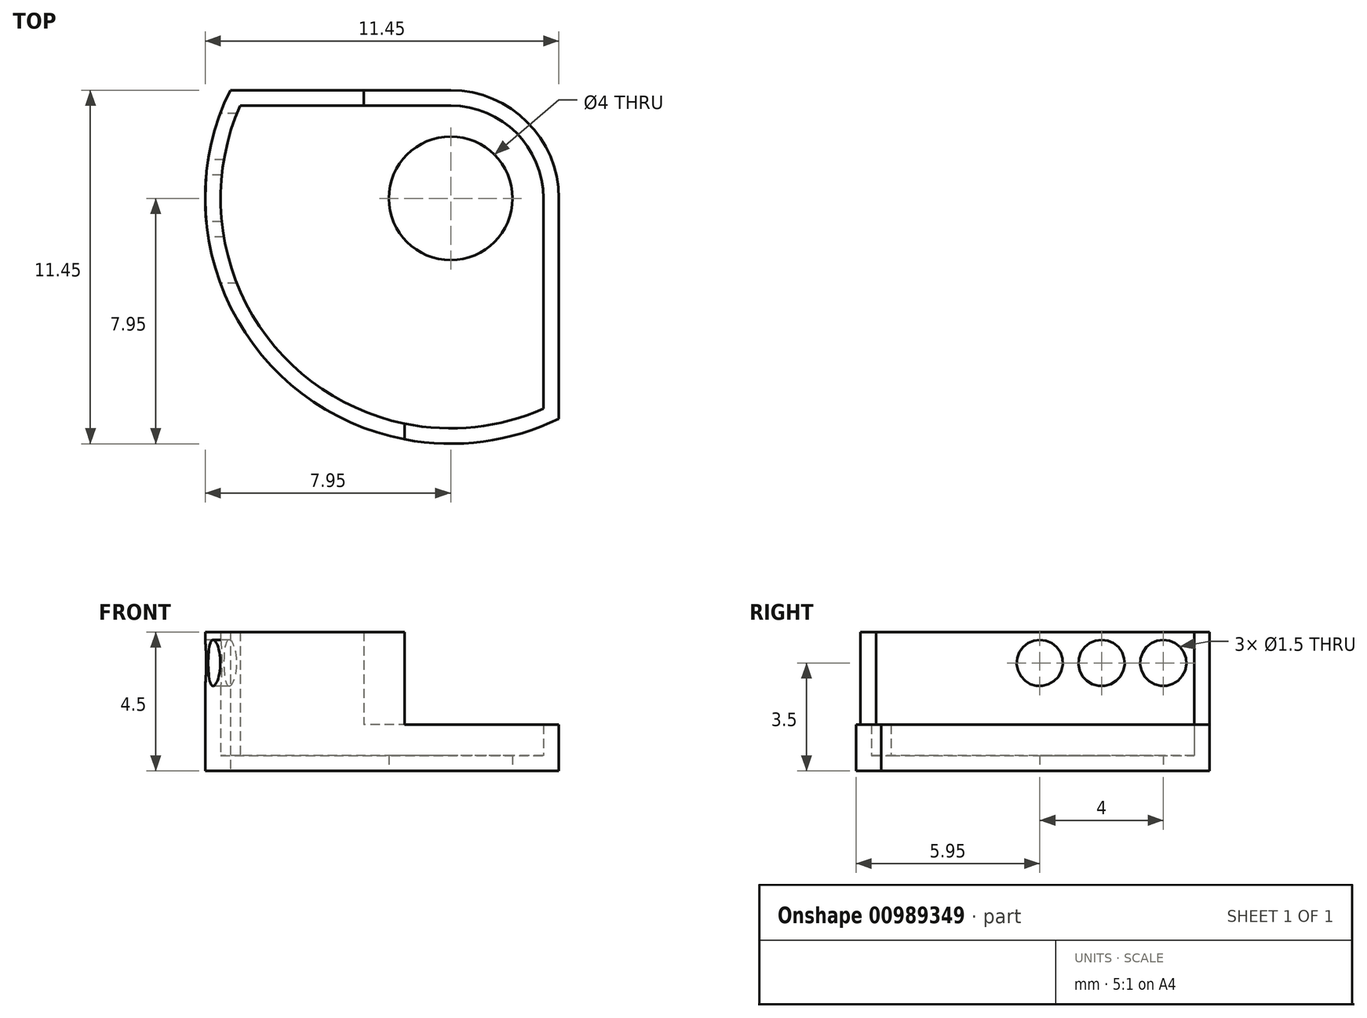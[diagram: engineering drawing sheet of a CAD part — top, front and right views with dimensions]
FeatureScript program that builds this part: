
annotation { "Feature Type Name" : "Feature", "Feature Type Description" : "" }
export const myFeature = defineFeature(function(context is Context, id is Id, definition is map)
    precondition{}
    {
        {
            var Q0;
            Q0=qCreatedBy(makeId("Top.planeOp"),FACE);
            var sketch = newSketch(context, id + "F0", { "sketchPlane" : qUnion([Q0])});
            skCircle(sketch, "E0", {"center": v(0, 0) * mm, "radius": 3.5 * mm});
            skCircle(sketch, "E1", {"center": v(0, 0) * mm, "radius": 7.95 * mm});
            skCircle(sketch, "E2", {"center": v(0, 0) * mm, "radius": 2 * mm});
            skLineSegment(sketch, "E3", {"start": v(3.5, 0) * mm, "end": v(3.5, -7.14) * mm});
            skLineSegment(sketch, "E4", {"start": v(0, 3.5) * mm, "end": v(-7.14, 3.5) * mm});
            skCircle(sketch, "E5", {"center": v(0, 0) * mm, "radius": 7.45 * mm});
            skCircle(sketch, "E6", {"center": v(0, 0) * mm, "radius": 3 * mm});
            skLineSegment(sketch, "E7", {"start": v(3, 0) * mm, "end": v(3, -6.82) * mm});
            skLineSegment(sketch, "E8", {"start": v(0, 3) * mm, "end": v(-6.82, 3) * mm});
            skLineSegment(sketch, "E9", {"start": v(-2.82, 3.5) * mm, "end": v(-2.82, 3) * mm});
            skLineSegment(sketch, "E10", {"start": v(-1.5, -7.3) * mm, "end": v(-1.5, -7.8) * mm});
            skSolve(sketch);
        }
        {
            var Q0;
            {var subQ0=sQuery(id+"F0.wireOp",EDGE,"E0");var subQ1=makeQuery(id+"F0.imprint","INTERSECT",VERTEX,{"derivedFrom":[subQ0,sQuery(id+"F0.wireOp",EDGE,"E3")]});Q0=makeQuery(id+"F0.imprint","IMPRINT",FACE,{"disambiguationData":[TD([[makeQuery(id+"F0.imprint","IMPRINT",EDGE,{"disambiguationData":[TD([[subQ1,-1.0]])],"derivedFrom":subQ0}),1.0]])]});}
            var Q1;
            {var subQ0=sQuery(id+"F0.wireOp",EDGE,"E4");var subQ1=sQuery(id+"F0.wireOp",EDGE,"E0");var subQ2=makeQuery(id+"F0.imprint","INTERSECT",VERTEX,{"derivedFrom":[subQ1,subQ0]});Q1=makeQuery(id+"F0.imprint","IMPRINT",FACE,{"disambiguationData":[TD([[makeQuery(id+"F0.imprint","IMPRINT",EDGE,{"disambiguationData":[TD([[subQ2,-1.0]])],"derivedFrom":subQ1}),-1.0]])]});}
            var Q2;
            {var subQ4=sQuery(id+"F0.wireOp",EDGE,"E1");var subQ6=sQuery(id+"F0.wireOp",EDGE,"E3");var subQ7=makeQuery(id+"F0.imprint","INTERSECT",VERTEX,{"derivedFrom":[subQ4,subQ6]});Q2=makeQuery(id+"F0.imprint","IMPRINT",FACE,{"disambiguationData":[TD([[makeQuery(id+"F0.imprint","IMPRINT",EDGE,{"disambiguationData":[TD([[subQ7,1.0]])],"derivedFrom":subQ4}),1.0]])]});}
            var Q3;
            {var subQ0=sQuery(id+"F0.wireOp",EDGE,"E3");var subQ1=sQuery(id+"F0.wireOp",EDGE,"E0");var subQ2=makeQuery(id+"F0.imprint","INTERSECT",VERTEX,{"derivedFrom":[subQ1,subQ0]});Q3=makeQuery(id+"F0.imprint","IMPRINT",FACE,{"disambiguationData":[TD([[makeQuery(id+"F0.imprint","IMPRINT",EDGE,{"disambiguationData":[TD([[subQ2,1.0]])],"derivedFrom":subQ1}),-1.0]])]});}
            var Q4;
            {var subQ0=sQuery(id+"F0.wireOp",EDGE,"lqIvwdBp-w5xU-ZFys-Ap5h-itLo7RTd6FTw");var subQ1=sQuery(id+"F0.wireOp",EDGE,"E0");var subQ2=makeQuery(id+"F0.imprint","INTERSECT",VERTEX,{"derivedFrom":[subQ1,subQ0]});Q4=makeQuery(id+"F0.imprint","IMPRINT",FACE,{"disambiguationData":[TD([[makeQuery(id+"F0.imprint","IMPRINT",EDGE,{"disambiguationData":[TD([[subQ2,-1.0]])],"derivedFrom":subQ1}),1.0]])]});}
            var Q5;
            {var subQ0=sQuery(id+"F0.wireOp",EDGE,"E4");var subQ1=sQuery(id+"F0.wireOp",EDGE,"E0");var subQ2=makeQuery(id+"F0.imprint","INTERSECT",VERTEX,{"derivedFrom":[subQ1,subQ0]});Q5=makeQuery(id+"F0.imprint","IMPRINT",FACE,{"disambiguationData":[TD([[makeQuery(id+"F0.imprint","IMPRINT",EDGE,{"disambiguationData":[TD([[subQ2,-1.0]])],"derivedFrom":subQ1}),-1.0]])]});}
            var Q6;
            {var subQ0=sQuery(id+"F0.wireOp",EDGE,"E8");var subQ1=sQuery(id+"F0.wireOp",EDGE,"E0");var subQ2=makeQuery(id+"F0.imprint","INTERSECT",VERTEX,{"derivedFrom":[subQ1,subQ0]});Q6=makeQuery(id+"F0.imprint","IMPRINT",FACE,{"disambiguationData":[TD([[makeQuery(id+"F0.imprint","IMPRINT",EDGE,{"disambiguationData":[TD([[subQ2,-1.0]])],"derivedFrom":subQ1}),-1.0]])]});}
            var Q7;
            {var subQ0=sQuery(id+"F0.wireOp",EDGE,"E3");var subQ1=sQuery(id+"F0.wireOp",EDGE,"E0");var subQ2=makeQuery(id+"F0.imprint","INTERSECT",VERTEX,{"derivedFrom":[subQ1,subQ0]});Q7=makeQuery(id+"F0.imprint","IMPRINT",FACE,{"disambiguationData":[TD([[makeQuery(id+"F0.imprint","IMPRINT",EDGE,{"disambiguationData":[TD([[subQ2,1.0]])],"derivedFrom":subQ1}),-1.0]])]});}
            var Q8;
            {var subQ0=sQuery(id+"F0.wireOp",EDGE,"E8");var subQ1=sQuery(id+"F0.wireOp",EDGE,"E0");var subQ2=makeQuery(id+"F0.imprint","INTERSECT",VERTEX,{"derivedFrom":[subQ1,subQ0]});Q8=makeQuery(id+"F0.imprint","IMPRINT",FACE,{"disambiguationData":[TD([[makeQuery(id+"F0.imprint","IMPRINT",EDGE,{"disambiguationData":[TD([[subQ2,-1.0]])],"derivedFrom":subQ1}),1.0]])]});}
            var Q9;
            Q9=makeQuery(id+"F0.imprint","IMPRINT",FACE,{"disambiguationData":[TD([[makeQuery(id+"F0.imprint","IMPRINT",EDGE,{"derivedFrom":sQuery(id+"F0.wireOp",EDGE,"E2")}),-1.0]])]});
            extrude(context, id + "F1", {"entities" : qUnion([Q0, Q1, Q2, Q3, Q4, Q5, Q6, Q7, Q8, Q9]), "depth" : .5 * mm, "offsetDistance" : 25 * mm});
        }
        {
            var Q0;
            {var subQ4=sQuery(id+"F0.wireOp",EDGE,"E1");var subQ6=sQuery(id+"F0.wireOp",EDGE,"E3");var subQ7=makeQuery(id+"F0.imprint","INTERSECT",VERTEX,{"derivedFrom":[subQ4,subQ6]});Q0=makeQuery(id+"F0.imprint","IMPRINT",FACE,{"disambiguationData":[TD([[makeQuery(id+"F0.imprint","IMPRINT",EDGE,{"disambiguationData":[TD([[subQ7,1.0]])],"derivedFrom":subQ4}),1.0]])]});}
            var Q1;
            {var subQ0=sQuery(id+"F0.wireOp",EDGE,"E3");var subQ1=sQuery(id+"F0.wireOp",EDGE,"E0");var subQ2=makeQuery(id+"F0.imprint","INTERSECT",VERTEX,{"derivedFrom":[subQ1,subQ0]});Q1=makeQuery(id+"F0.imprint","IMPRINT",FACE,{"disambiguationData":[TD([[makeQuery(id+"F0.imprint","IMPRINT",EDGE,{"disambiguationData":[TD([[subQ2,1.0]])],"derivedFrom":subQ1}),-1.0]])]});}
            var Q2;
            {var subQ0=sQuery(id+"F0.wireOp",EDGE,"E0");var subQ1=makeQuery(id+"F0.imprint","INTERSECT",VERTEX,{"derivedFrom":[subQ0,sQuery(id+"F0.wireOp",EDGE,"E3")]});Q2=makeQuery(id+"F0.imprint","IMPRINT",FACE,{"disambiguationData":[TD([[makeQuery(id+"F0.imprint","IMPRINT",EDGE,{"disambiguationData":[TD([[subQ1,-1.0]])],"derivedFrom":subQ0}),1.0]])]});}
            var Q3;
            {var subQ0=sQuery(id+"F0.wireOp",EDGE,"E4");var subQ1=sQuery(id+"F0.wireOp",EDGE,"E0");var subQ2=makeQuery(id+"F0.imprint","INTERSECT",VERTEX,{"derivedFrom":[subQ1,subQ0]});Q3=makeQuery(id+"F0.imprint","IMPRINT",FACE,{"disambiguationData":[TD([[makeQuery(id+"F0.imprint","IMPRINT",EDGE,{"disambiguationData":[TD([[subQ2,-1.0]])],"derivedFrom":subQ1}),-1.0]])]});}
            var Q4;
            {var subQ0=sQuery(id+"F0.wireOp",EDGE,"E9");Q4=makeQuery(id+"F0.imprint","IMPRINT",FACE,{"disambiguationData":[TD([[makeQuery(id+"F0.imprint","IMPRINT",EDGE,{"derivedFrom":subQ0}),-1.0]])]});}
            var Q5;
            {var subQ6=sQuery(id+"F0.wireOp",EDGE,"E10");Q5=makeQuery(id+"F0.imprint","IMPRINT",FACE,{"disambiguationData":[TD([[makeQuery(id+"F0.imprint","IMPRINT",EDGE,{"derivedFrom":subQ6}),-1.0]])]});}
            var Q6;
            {var subQ0=sQuery(id+"F0.wireOp",EDGE,"E4");var subQ1=sQuery(id+"F0.wireOp",EDGE,"E1");var subQ2=makeQuery(id+"F0.imprint","INTERSECT",VERTEX,{"derivedFrom":[subQ1,subQ0]});Q6=makeQuery(id+"F0.imprint","IMPRINT",FACE,{"disambiguationData":[TD([[makeQuery(id+"F0.imprint","IMPRINT",EDGE,{"disambiguationData":[TD([[subQ2,-1.0]])],"derivedFrom":subQ1}),1.0]])]});}
            extrude(context, id + "F2", {"entities" : qUnion([Q0, Q1, Q2, Q3, Q4, Q5, Q6]), "operationType" : NewBodyOperationType.ADD, "depth" : 1.5 * mm, "offsetDistance" : 25 * mm});
        }
        {
            var Q0;
            {var subQ0=sQuery(id+"F0.wireOp",EDGE,"E4");var subQ1=sQuery(id+"F0.wireOp",EDGE,"E1");var subQ2=makeQuery(id+"F0.imprint","INTERSECT",VERTEX,{"derivedFrom":[subQ1,subQ0]});Q0=makeQuery(id+"F0.imprint","IMPRINT",FACE,{"disambiguationData":[TD([[makeQuery(id+"F0.imprint","IMPRINT",EDGE,{"disambiguationData":[TD([[subQ2,-1.0]])],"derivedFrom":subQ1}),1.0]])]});}
            var Q1;
            {var subQ0=sQuery(id+"F0.wireOp",EDGE,"E9");var subQ1=sQuery(id+"F0.wireOp",EDGE,"E4");var subQ2=makeQuery(id+"F0.imprint","INTERSECT",VERTEX,{"derivedFrom":[subQ1,subQ0]});Q1=makeQuery(id+"F0.imprint","IMPRINT",FACE,{"disambiguationData":[TD([[makeQuery(id+"F0.imprint","IMPRINT",EDGE,{"disambiguationData":[TD([[subQ2,-1.0]])],"derivedFrom":subQ1}),1.0]])]});}
            var Q2;
            {var subQ0=sQuery(id+"F0.wireOp",EDGE,"E10");Q2=makeQuery(id+"F0.imprint","IMPRINT",FACE,{"disambiguationData":[TD([[makeQuery(id+"F0.imprint","IMPRINT",EDGE,{"derivedFrom":subQ0}),-1.0]])]});}
            extrude(context, id + "F3", {"entities" : qUnion([Q0, Q1, Q2]), "operationType" : NewBodyOperationType.ADD, "depth" : 4.5 * mm, "offsetDistance" : 25 * mm});
        }
        {
            var Q0;
            Q0=makeQuery(id+"F3.opExtrude","CAP_VERTEX",VERTEX,{"disambiguationData":[OSD([sQuery(id+"F0.wireOp",EDGE,"E1"),sQuery(id+"F0.wireOp",EDGE,"E4")])],"isStart":false});
            var Q1;
            Q1=qCreatedBy(makeId("Right.planeOp"),FACE);
            cPlane(context, id + "F4", {"entities" : qUnion([Q0, Q1]), "cplaneType" : CPlaneType.PLANE_POINT, "offset" : 25 * mm, "width" : 150 * mm, "height" : 150 * mm});
        }
        {
            var Q0;
            Q0=qCreatedBy(id+"F4.planeOp",FACE);
            var sketch = newSketch(context, id + "F5", { "sketchPlane" : qUnion([Q0])});
            skLineSegment(sketch, "E11", {"start": v(0, 0) * mm, "end": v(0, 3.5) * mm});
            skLineSegment(sketch, "E12", {"start": v(0, 3.5) * mm, "end": v(-2, 3.5) * mm});
            skLineSegment(sketch, "E13", {"start": v(0, 3.5) * mm, "end": v(2, 3.5) * mm});
            skCircle(sketch, "E14", {"center": v(2, 3.5) * mm, "radius": 0.75 * mm});
            skCircle(sketch, "E15", {"center": v(0, 3.5) * mm, "radius": 0.75 * mm});
            skCircle(sketch, "E16", {"center": v(-2, 3.5) * mm, "radius": 0.75 * mm});
            skSolve(sketch);
        }
        {
            var Q0;
            Q0=makeQuery(id+"F5.imprint","IMPRINT",FACE,{"disambiguationData":[TD([[makeQuery(id+"F5.imprint","IMPRINT",EDGE,{"derivedFrom":sQuery(id+"F5.wireOp",EDGE,"E14")}),1.0]])]});
            var Q1;
            {var subQ1=sQuery(id+"F5.wireOp",EDGE,"E11");var subQ3=sQuery(id+"F5.wireOp",EDGE,"E15");var subQ4=makeQuery(id+"F5.imprint","INTERSECT",VERTEX,{"derivedFrom":[subQ1,subQ3]});Q1=makeQuery(id+"F5.imprint","IMPRINT",FACE,{"disambiguationData":[TD([[makeQuery(id+"F5.imprint","IMPRINT",EDGE,{"disambiguationData":[TD([[subQ4,-1.0]])],"derivedFrom":subQ3}),1.0]])]});}
            var Q2;
            {var subQ1=sQuery(id+"F5.wireOp",EDGE,"E12");var subQ3=sQuery(id+"F5.wireOp",EDGE,"E15");var subQ4=makeQuery(id+"F5.imprint","INTERSECT",VERTEX,{"derivedFrom":[subQ1,subQ3]});Q2=makeQuery(id+"F5.imprint","IMPRINT",FACE,{"disambiguationData":[TD([[makeQuery(id+"F5.imprint","IMPRINT",EDGE,{"disambiguationData":[TD([[subQ4,1.0]])],"derivedFrom":subQ3}),1.0]])]});}
            var Q3;
            {var subQ1=sQuery(id+"F5.wireOp",EDGE,"E11");var subQ3=sQuery(id+"F5.wireOp",EDGE,"E15");var subQ4=makeQuery(id+"F5.imprint","INTERSECT",VERTEX,{"derivedFrom":[subQ1,subQ3]});Q3=makeQuery(id+"F5.imprint","IMPRINT",FACE,{"disambiguationData":[TD([[makeQuery(id+"F5.imprint","IMPRINT",EDGE,{"disambiguationData":[TD([[subQ4,1.0]])],"derivedFrom":subQ3}),1.0]])]});}
            var Q4;
            Q4=makeQuery(id+"F5.imprint","IMPRINT",FACE,{"disambiguationData":[TD([[makeQuery(id+"F5.imprint","IMPRINT",EDGE,{"derivedFrom":sQuery(id+"F5.wireOp",EDGE,"E16")}),1.0]])]});
            var Q5;
            {var subQ0=sQuery(id+"F0.wireOp",EDGE,"E5");Q5=makeQuery(id+"F3.boolean.opBoolean","MERGE",FACE,{"derivedFrom":[makeQuery(id+"F2.opExtrude","SWEPT_FACE",FACE,{"disambiguationData":[OSD([subQ0])]}),makeQuery(id+"F3.opExtrude","SWEPT_FACE",FACE,{"disambiguationData":[OSD([subQ0])]})]});}
            var Q6;
            {var subQ0=sQuery(id+"F0.wireOp",EDGE,"E1");Q6=makeQuery(id+"F3.boolean.opBoolean","MERGE",FACE,{"derivedFrom":[makeQuery(id+"F2.boolean.opBoolean","MERGE",FACE,{"derivedFrom":[makeQuery(id+"F1.opExtrude","SWEPT_FACE",FACE,{"disambiguationData":[OSD([subQ0])]}),makeQuery(id+"F2.opExtrude","SWEPT_FACE",FACE,{"disambiguationData":[OSD([subQ0])]})]}),makeQuery(id+"F3.opExtrude","SWEPT_FACE",FACE,{"disambiguationData":[OSD([subQ0])]})]});}
            extrude(context, id + "F6", {"entities" : qUnion([Q0, Q1, Q2, Q3, Q4]), "operationType" : NewBodyOperationType.REMOVE, "endBound" : BoundingType.UP_TO_SURFACE, "depth" : .1 * mm, "endBoundEntityFace" : qUnion([Q5]), "offsetDistance" : 25 * mm, "hasSecondDirection" : true, "secondDirectionBound" : SecondDirectionBoundingType.UP_TO_SURFACE, "secondDirectionOppositeDirection" : true, "secondDirectionDepth" : 25 * mm, "secondDirectionBoundEntityFace" : qUnion([Q6])});
        }
    });
